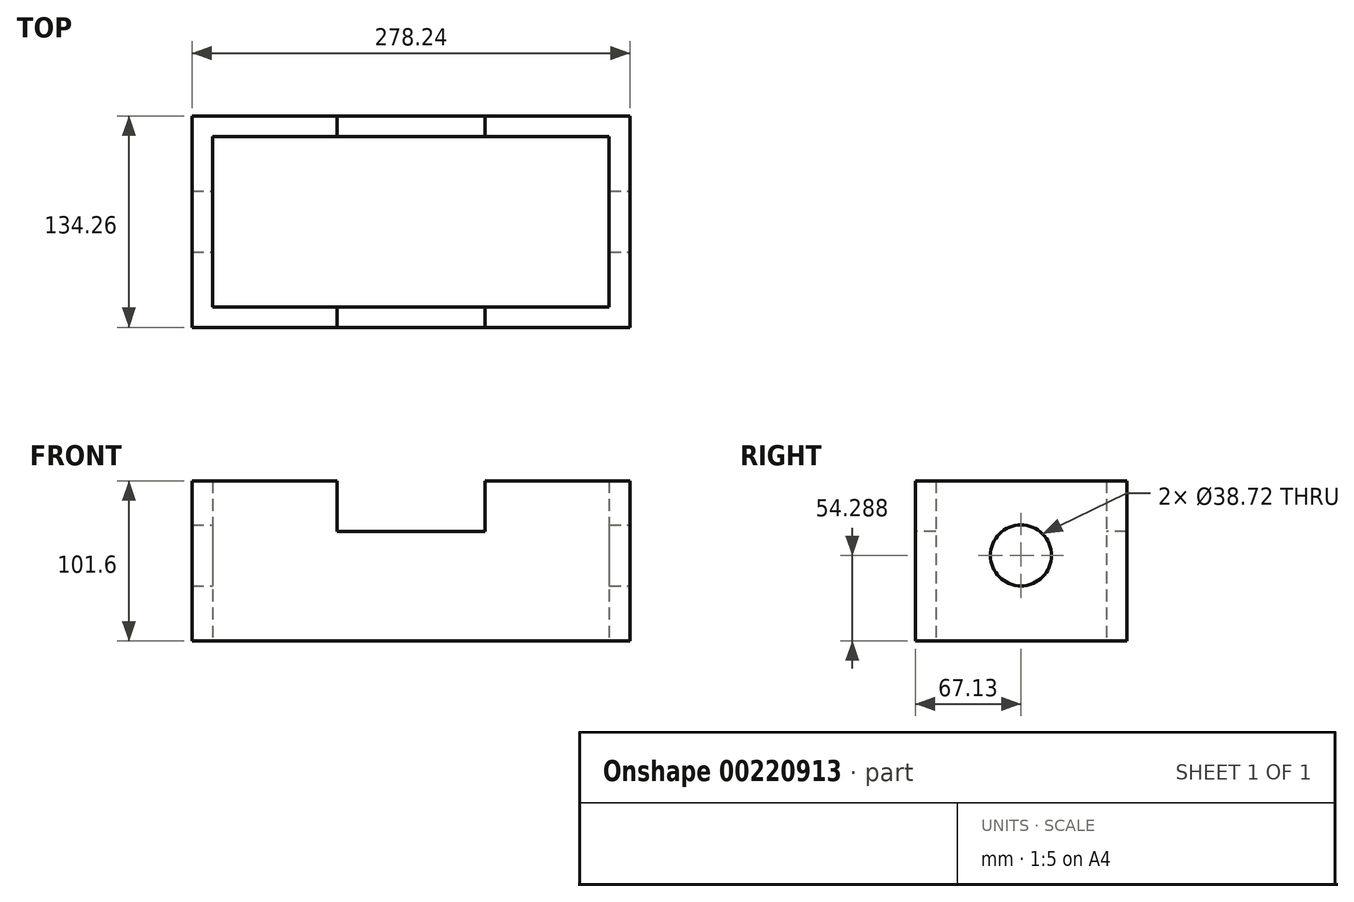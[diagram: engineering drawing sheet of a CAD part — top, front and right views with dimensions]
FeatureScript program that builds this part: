
annotation { "Feature Type Name" : "Feature", "Feature Type Description" : "" }
export const myFeature = defineFeature(function(context is Context, id is Id, definition is map)
    precondition{}
    {
        {
            var Q0;
            Q0=qCreatedBy(makeId("Top.planeOp"),FACE);
            var sketch = newSketch(context, id + "F0", { "sketchPlane" : qUnion([Q0])});
            skLineSegment(sketch, "E0.bottom", {"start": v(139.12, -67.13) * mm, "end": v(-139.12, -67.13) * mm});
            skLineSegment(sketch, "E0.top", {"start": v(139.12, 67.13) * mm, "end": v(-139.12, 67.13) * mm});
            skLineSegment(sketch, "E0.left", {"start": v(139.12, -67.13) * mm, "end": v(139.12, 67.13) * mm});
            skLineSegment(sketch, "E0.right", {"start": v(-139.12, -67.13) * mm, "end": v(-139.12, 67.13) * mm});
            skPoint(sketch, "E0.middle", {"position": v(0, 0) * mm});
            skLineSegment(sketch, "E1.bottom", {"start": v(125.84, -54.14) * mm, "end": v(-125.84, -54.14) * mm});
            skLineSegment(sketch, "E1.top", {"start": v(125.84, 54.14) * mm, "end": v(-125.84, 54.14) * mm});
            skLineSegment(sketch, "E1.left", {"start": v(125.84, -54.14) * mm, "end": v(125.84, 54.14) * mm});
            skLineSegment(sketch, "E1.right", {"start": v(-125.84, -54.14) * mm, "end": v(-125.84, 54.14) * mm});
            skSolve(sketch);
        }
        {
            var Q0;
            Q0=makeQuery(id+"F0.imprint","IMPRINT",FACE,{"disambiguationData":[TD([[makeQuery(id+"F0.imprint","IMPRINT",EDGE,{"derivedFrom":sQuery(id+"F0.wireOp",EDGE,"E0.bottom")}),-1.0]])]});
            extrude(context, id + "F1", {"entities" : qUnion([Q0]), "depth" : 101.6 * mm});
        }
        {
            var Q0;
            Q0=makeQuery(id+"F1.opExtrude","SWEPT_FACE",FACE,{"disambiguationData":[OSD([sQuery(id+"F0.wireOp",EDGE,"E0.left")])]});
            var sketch = newSketch(context, id + "F2", { "sketchPlane" : qUnion([Q0])});
            skCircle(sketch, "E2", {"center": v(0, 54.29) * mm, "radius": 19.36 * mm});
            skSolve(sketch);
        }
        {
            var Q0;
            Q0=makeQuery(id+"F2.imprint","IMPRINT",FACE,{"disambiguationData":[TD([[makeQuery(id+"F2.imprint","IMPRINT",EDGE,{"derivedFrom":sQuery(id+"F2.wireOp",EDGE,"E2")}),1.0]])]});
            extrude(context, id + "F3", {"entities" : qUnion([Q0]), "operationType" : NewBodyOperationType.REMOVE, "endBound" : BoundingType.THROUGH_ALL, "oppositeDirection" : true, "depth" : 25.4 * mm});
        }
        {
            var Q0;
            Q0=makeQuery(id+"F1.opExtrude","SWEPT_FACE",FACE,{"disambiguationData":[OSD([sQuery(id+"F0.wireOp",EDGE,"E0.bottom")])]});
            var sketch = newSketch(context, id + "F4", { "sketchPlane" : qUnion([Q0])});
            skLineSegment(sketch, "E3.bottom", {"start": v(-46.95, 101.6) * mm, "end": v(46.95, 101.6) * mm});
            skLineSegment(sketch, "E3.top", {"start": v(-46.95, 69.65) * mm, "end": v(46.95, 69.65) * mm});
            skLineSegment(sketch, "E3.left", {"start": v(-46.95, 101.6) * mm, "end": v(-46.95, 69.65) * mm});
            skLineSegment(sketch, "E3.right", {"start": v(46.95, 101.6) * mm, "end": v(46.95, 69.65) * mm});
            skPoint(sketch, "E3.middle", {"position": v(0, 85.62) * mm});
            skPoint(sketch, "E3.middle.positionSnap0", {"position": v(0, 101.6) * mm});
            skPoint(sketch, "E3.centerSnap0", {"position": v(0, 101.6) * mm});
            skSolve(sketch);
        }
        {
            var Q0;
            Q0=makeQuery(id+"F4.imprint","IMPRINT",FACE,{"disambiguationData":[TD([[makeQuery(id+"F4.imprint","IMPRINT",EDGE,{"derivedFrom":sQuery(id+"F4.wireOp",EDGE,"E3.bottom")}),1.0]])]});
            extrude(context, id + "F5", {"entities" : qUnion([Q0]), "operationType" : NewBodyOperationType.REMOVE, "endBound" : BoundingType.THROUGH_ALL, "oppositeDirection" : true, "depth" : 25.4 * mm});
        }
    });
